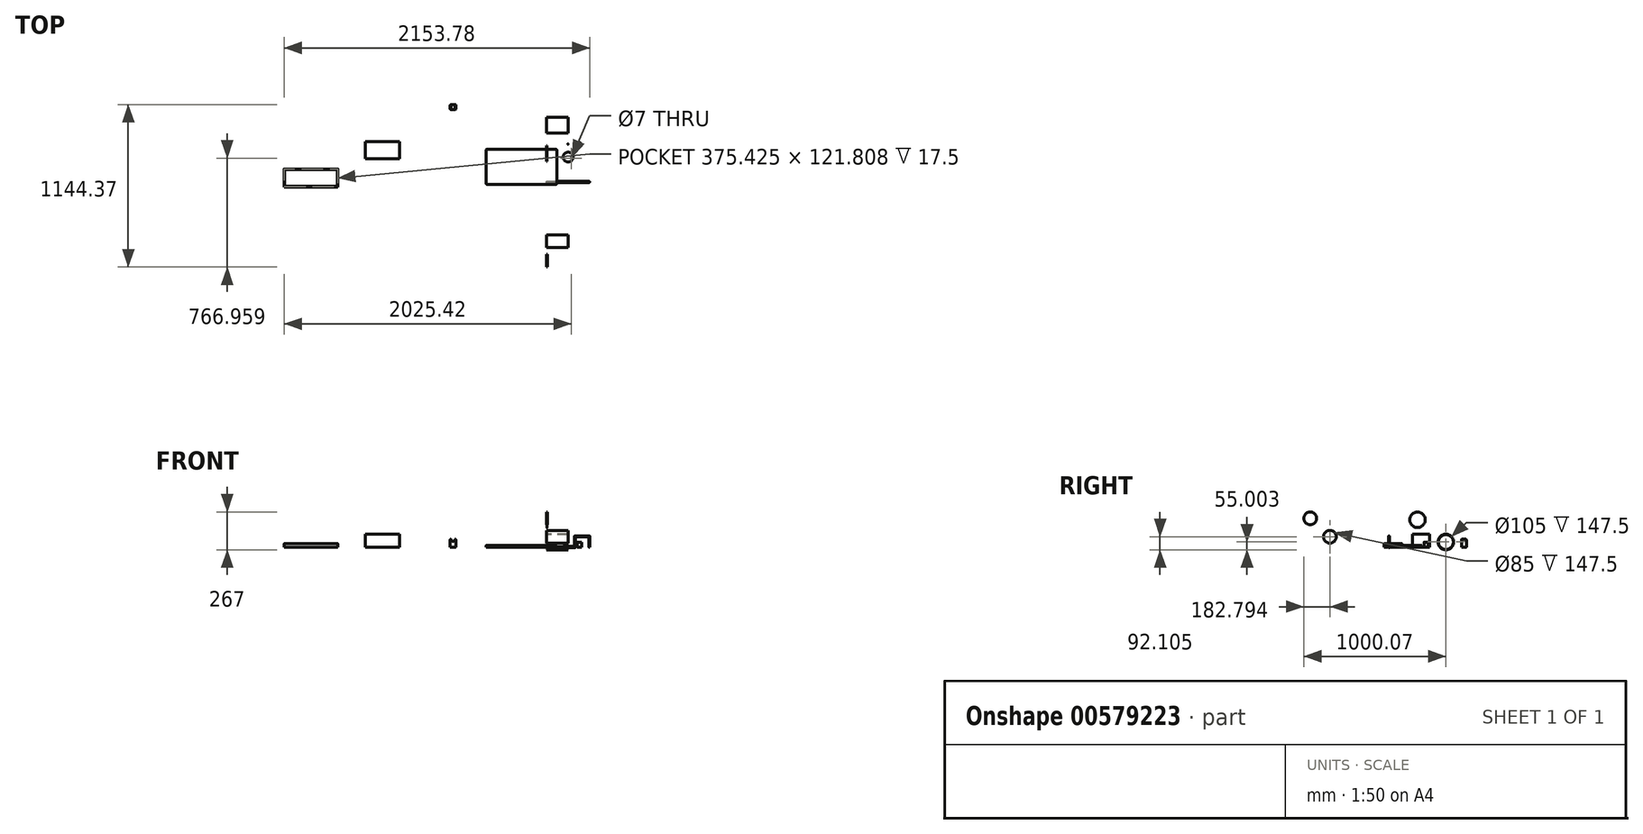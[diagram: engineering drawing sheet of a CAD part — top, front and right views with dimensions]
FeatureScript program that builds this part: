
annotation { "Feature Type Name" : "Feature", "Feature Type Description" : "" }
export const myFeature = defineFeature(function(context is Context, id is Id, definition is map)
    precondition{}
    {
        {
            var Q0;
            Q0=qCreatedBy(makeId("Top.planeOp"),FACE);
            var sketch = newSketch(context, id + "F0", { "sketchPlane" : qUnion([Q0])});
            skLineSegment(sketch, "E0.bottom", {"start": v(-427.44, 231.54) * mm, "end": v(72.56, 231.54) * mm});
            skLineSegment(sketch, "E0.top", {"start": v(-427.44, -18.46) * mm, "end": v(72.56, -18.46) * mm});
            skLineSegment(sketch, "E0.left", {"start": v(-427.44, 231.54) * mm, "end": v(-427.44, -18.46) * mm});
            skLineSegment(sketch, "E0.right", {"start": v(72.56, 231.54) * mm, "end": v(72.56, -18.46) * mm});
            skSolve(sketch);
        }
        {
            var Q0;
            Q0=makeQuery(id+"F0.imprint","IMPRINT",FACE,{"disambiguationData":[TD([[makeQuery(id+"F0.imprint","IMPRINT",EDGE,{"derivedFrom":sQuery(id+"F0.wireOp",EDGE,"E0.bottom")}),-1.0]])]});
            extrude(context, id + "F1", {"entities" : qUnion([Q0]), "depth" : 10 * mm, "offsetDistance" : 25 * mm});
        }
        {
            var Q0;
            Q0=qCreatedBy(makeId("Right.planeOp"),FACE);
            var sketch = newSketch(context, id + "F2", { "sketchPlane" : qUnion([Q0])});
            skCircle(sketch, "E1", {"center": v(400.53, 35.64) * mm, "radius": 55 * mm});
            skSolve(sketch);
        }
        {
            var Q0;
            Q0=makeQuery(id+"F2.imprint","IMPRINT",FACE,{"disambiguationData":[TD([[makeQuery(id+"F2.imprint","IMPRINT",EDGE,{"derivedFrom":sQuery(id+"F2.wireOp",EDGE,"E1")}),1.0]])]});
            extrude(context, id + "F3", {"entities" : qUnion([Q0]), "depth" : 150 * mm, "offsetDistance" : 25 * mm});
        }
        {
            var Q0;
            Q0=makeQuery(id+"F3.opExtrude","CAP_FACE",FACE,{"disambiguationData":[OSD([sQuery(id+"F2.wireOp",EDGE,"E1")])],"isStart":false});
            shell(context, id + "F4", {"entities" : qUnion([Q0]), "thickness" : 2.5 * mm});
        }
        {
            var Q0;
            Q0=makeQuery(id+"F1.opExtrude","SWEPT_EDGE",EDGE,{"disambiguationData":[OSD([sQuery(id+"F0.wireOp",EDGE,"E0.bottom"),sQuery(id+"F0.wireOp",EDGE,"E0.right")])]});
            var Q1;
            Q1=makeQuery(id+"F1.opExtrude","SWEPT_EDGE",EDGE,{"disambiguationData":[OSD([sQuery(id+"F0.wireOp",EDGE,"E0.bottom"),sQuery(id+"F0.wireOp",EDGE,"E0.left")])]});
            var Q2;
            Q2=makeQuery(id+"F1.opExtrude","SWEPT_EDGE",EDGE,{"disambiguationData":[OSD([sQuery(id+"F0.wireOp",EDGE,"E0.top"),sQuery(id+"F0.wireOp",EDGE,"E0.left")])]});
            var Q3;
            Q3=makeQuery(id+"F1.opExtrude","SWEPT_EDGE",EDGE,{"disambiguationData":[OSD([sQuery(id+"F0.wireOp",EDGE,"E0.top"),sQuery(id+"F0.wireOp",EDGE,"E0.right")])]});
            fillet(context, id + "F5", {"entities" : qUnion([Q0, Q1, Q2, Q3]), "radius" : 10 * mm, "tangentPropagation" : true, "allowEdgeOverflow" : false});
        }
        {
            var Q0;
            Q0=qCreatedBy(makeId("Right.planeOp"),FACE);
            var sketch = newSketch(context, id + "F6", { "sketchPlane" : qUnion([Q0])});
            skCircle(sketch, "E2", {"center": v(200.54, 191.77) * mm, "radius": 54.75 * mm});
            skSolve(sketch);
        }
        {
            var Q0;
            Q0 = qSketchRegion(id + "F6", true);
            extrude(context, id + "F7", {"entities" : qUnion([Q0]), "depth" : 3 * mm, "offsetDistance" : 25 * mm});
        }
        {
            var Q0;
            Q0=qCreatedBy(makeId("Front.planeOp"),FACE);
            var sketch = newSketch(context, id + "F8", { "sketchPlane" : qUnion([Q0])});
            skLineSegment(sketch, "E3", {"start": v(0, 0) * mm, "end": v(200, 0) * mm});
            skLineSegment(sketch, "E4", {"start": v(200, 0) * mm, "end": v(200, 75) * mm});
            skLineSegment(sketch, "E5", {"start": v(200, 75) * mm, "end": v(300, 75) * mm});
            skLineSegment(sketch, "E6", {"start": v(300, 75) * mm, "end": v(300, 0) * mm});
            skSolve(sketch);
        }
        {
            var Q0;
            Q0=qCreatedBy(makeId("Right.planeOp"),FACE);
            var sketch = newSketch(context, id + "F9", { "sketchPlane" : qUnion([Q0])});
            skCircle(sketch, "E7", {"center": v(0, 0) * mm, "radius": 3.5 * mm});
            skSolve(sketch);
        }
        {
            var Q0;
            Q0=makeQuery(id+"F9.imprint","IMPRINT",FACE,{"disambiguationData":[TD([[makeQuery(id+"F9.imprint","IMPRINT",EDGE,{"derivedFrom":sQuery(id+"F9.wireOp",EDGE,"E7")}),1.0]])]});
            var Q1;
            Q1=sQuery(id+"F8.wireOp",EDGE,"E3");
            var Q2;
            Q2=sQuery(id+"F8.wireOp",EDGE,"E4");
            var Q3;
            Q3=sQuery(id+"F8.wireOp",EDGE,"E5");
            var Q4;
            Q4=sQuery(id+"F8.wireOp",EDGE,"E6");
            sweep(context, id + "F10", {"profiles" : qUnion([Q0]), "path" : qUnion([Q1, Q2, Q3, Q4])});
        }
        {
            var Q0;
            Q0=qCreatedBy(makeId("Top.planeOp"),FACE);
            var sketch = newSketch(context, id + "F11", { "sketchPlane" : qUnion([Q0])});
            skCircle(sketch, "E8", {"center": v(151.31, 175.12) * mm, "radius": 35 * mm});
            skSolve(sketch);
        }
        {
            var Q0;
            Q0=makeQuery(id+"F11.imprint","IMPRINT",FACE,{"disambiguationData":[TD([[makeQuery(id+"F11.imprint","IMPRINT",EDGE,{"derivedFrom":sQuery(id+"F11.wireOp",EDGE,"E8")}),1.0]])]});
            extrude(context, id + "F12", {"entities" : qUnion([Q0]), "depth" : 5 * mm, "offsetDistance" : 25 * mm});
        }
        {
            var Q0;
            Q0=qCreatedBy(makeId("Top.planeOp"),FACE);
            var sketch = newSketch(context, id + "F13", { "sketchPlane" : qUnion([Q0])});
            skCircle(sketch, "E9", {"center": v(230.62, 261.74) * mm, "radius": 15 * mm});
            skSolve(sketch);
        }
        {
            var Q0;
            Q0=makeQuery(id+"F13.imprint","IMPRINT",FACE,{"disambiguationData":[TD([[makeQuery(id+"F13.imprint","IMPRINT",EDGE,{"derivedFrom":sQuery(id+"F13.wireOp",EDGE,"E9")}),1.0]])]});
            extrude(context, id + "F14", {"entities" : qUnion([Q0]), "depth" : 35 * mm, "offsetDistance" : 25 * mm});
        }
        {
            var Q0;
            Q0=qCreatedBy(makeId("Top.planeOp"),FACE);
            var sketch = newSketch(context, id + "F15", { "sketchPlane" : qUnion([Q0])});
            skCircle(sketch, "E10", {"center": v(150.44, 267.16) * mm, "radius": 2.5 * mm});
            skSolve(sketch);
        }
        {
            var Q0;
            Q0=makeQuery(id+"F15.imprint","IMPRINT",FACE,{"disambiguationData":[TD([[makeQuery(id+"F15.imprint","IMPRINT",EDGE,{"derivedFrom":sQuery(id+"F15.wireOp",EDGE,"E10")}),1.0]])]});
            extrude(context, id + "F16", {"entities" : qUnion([Q0]), "depth" : 5 * mm, "offsetDistance" : 25 * mm});
        }
        {
            var Q0;
            Q0=qCreatedBy(makeId("Top.planeOp"),FACE);
            var sketch = newSketch(context, id + "F17", { "sketchPlane" : qUnion([Q0])});
            skLineSegment(sketch, "E11.bottom", {"start": v(-639.12, 509.83) * mm, "end": v(-679.12, 509.83) * mm});
            skLineSegment(sketch, "E11.top", {"start": v(-639.12, 544.83) * mm, "end": v(-679.12, 544.83) * mm});
            skLineSegment(sketch, "E11.left", {"start": v(-639.12, 509.83) * mm, "end": v(-639.12, 544.83) * mm});
            skLineSegment(sketch, "E11.right", {"start": v(-679.12, 509.83) * mm, "end": v(-679.12, 544.83) * mm});
            skPoint(sketch, "E11.middle", {"position": v(-659.12, 527.33) * mm});
            skSolve(sketch);
        }
        {
            var Q0;
            Q0=makeQuery(id+"F17.imprint","IMPRINT",FACE,{"disambiguationData":[TD([[makeQuery(id+"F17.imprint","IMPRINT",EDGE,{"derivedFrom":sQuery(id+"F17.wireOp",EDGE,"E11.bottom")}),-1.0]])]});
            extrude(context, id + "F18", {"entities" : qUnion([Q0]), "depth" : 55 * mm, "offsetDistance" : 25 * mm});
        }
        {
            var Q0;
            Q0=makeQuery(id+"F18.opExtrude","SWEPT_FACE",FACE,{"disambiguationData":[OSD([sQuery(id+"F17.wireOp",EDGE,"E11.bottom")])]});
            var sketch = newSketch(context, id + "F19", { "sketchPlane" : qUnion([Q0])});
            skArc(sketch, "E12", {"start": v(-674.12, 55) * mm, "mid": v(-659.12, 39.88) * mm, "end": v(-644.12, 55) * mm});
            skSolve(sketch);
        }
        {
            var Q0;
            {var subQ0=sQuery(id+"F19.wireOp",EDGE,"E12");Q0=makeQuery(id+"F19.imprint","IMPRINT",FACE,{"disambiguationData":[TD([[makeQuery(id+"F19.imprint","IMPRINT",EDGE,{"derivedFrom":subQ0}),1.0]])]});}
            extrude(context, id + "F20", {"entities" : qUnion([Q0]), "operationType" : NewBodyOperationType.REMOVE, "oppositeDirection" : true, "depth" : 40 * mm, "offsetDistance" : 25 * mm});
        }
        {
            var Q0;
            Q0=makeQuery(id+"F18.opExtrude","CAP_EDGE",EDGE,{"disambiguationData":[OSD([sQuery(id+"F17.wireOp",EDGE,"E11.right")])],"isStart":false});
            var Q1;
            {var subQ0=sQuery(id+"F17.wireOp",EDGE,"E11.bottom");var subQ1=sQuery(id+"F17.wireOp",EDGE,"E11.right");Q1=makeQuery(id+"F20.boolean.opBoolean","SPLIT",EDGE,{"disambiguationData":[TD([makeQuery(id+"F18.opExtrude","SWEPT_FACE",FACE,{"disambiguationData":[OSD([subQ1])]})])],"derivedFrom":makeQuery(id+"F18.opExtrude","CAP_EDGE",EDGE,{"disambiguationData":[OSD([subQ0])],"isStart":false})});}
            var Q2;
            Q2=makeQuery(id+"F18.opExtrude","SWEPT_EDGE",EDGE,{"disambiguationData":[OSD([sQuery(id+"F17.wireOp",EDGE,"E11.bottom"),sQuery(id+"F17.wireOp",EDGE,"E11.right")])]});
            var Q3;
            Q3=makeQuery(id+"F18.opExtrude","SWEPT_EDGE",EDGE,{"disambiguationData":[OSD([sQuery(id+"F17.wireOp",EDGE,"E11.bottom"),sQuery(id+"F17.wireOp",EDGE,"E11.left")])]});
            var Q4;
            {var subQ0=sQuery(id+"F17.wireOp",EDGE,"E11.bottom");var subQ1=sQuery(id+"F17.wireOp",EDGE,"E11.left");Q4=makeQuery(id+"F20.boolean.opBoolean","SPLIT",EDGE,{"disambiguationData":[TD([makeQuery(id+"F18.opExtrude","SWEPT_FACE",FACE,{"disambiguationData":[OSD([subQ1])]})])],"derivedFrom":makeQuery(id+"F18.opExtrude","CAP_EDGE",EDGE,{"disambiguationData":[OSD([subQ0])],"isStart":false})});}
            var Q5;
            Q5=makeQuery(id+"F18.opExtrude","SWEPT_EDGE",EDGE,{"disambiguationData":[OSD([sQuery(id+"F17.wireOp",EDGE,"E11.top"),sQuery(id+"F17.wireOp",EDGE,"E11.left")])]});
            var Q6;
            Q6=makeQuery(id+"F18.opExtrude","CAP_EDGE",EDGE,{"disambiguationData":[OSD([sQuery(id+"F17.wireOp",EDGE,"E11.left")])],"isStart":false});
            var Q7;
            {var subQ0=sQuery(id+"F17.wireOp",EDGE,"E11.left");var subQ1=sQuery(id+"F17.wireOp",EDGE,"E11.top");Q7=makeQuery(id+"F20.boolean.opBoolean","SPLIT",EDGE,{"disambiguationData":[TD([makeQuery(id+"F18.opExtrude","SWEPT_FACE",FACE,{"disambiguationData":[OSD([subQ0])]})])],"derivedFrom":makeQuery(id+"F18.opExtrude","CAP_EDGE",EDGE,{"disambiguationData":[OSD([subQ1])],"isStart":false})});}
            var Q8;
            {var subQ0=sQuery(id+"F17.wireOp",EDGE,"E11.right");var subQ1=sQuery(id+"F17.wireOp",EDGE,"E11.top");Q8=makeQuery(id+"F20.boolean.opBoolean","SPLIT",EDGE,{"disambiguationData":[TD([makeQuery(id+"F18.opExtrude","SWEPT_FACE",FACE,{"disambiguationData":[OSD([subQ0])]})])],"derivedFrom":makeQuery(id+"F18.opExtrude","CAP_EDGE",EDGE,{"disambiguationData":[OSD([subQ1])],"isStart":false})});}
            var Q9;
            Q9=makeQuery(id+"F18.opExtrude","SWEPT_EDGE",EDGE,{"disambiguationData":[OSD([sQuery(id+"F17.wireOp",EDGE,"E11.top"),sQuery(id+"F17.wireOp",EDGE,"E11.right")])]});
            fillet(context, id + "F21", {"entities" : qUnion([Q0, Q1, Q2, Q3, Q4, Q5, Q6, Q7, Q8, Q9]), "radius" : 5 * mm, "tangentPropagation" : true, "allowEdgeOverflow" : false});
        }
        {
            var Q0;
            Q0=makeQuery(id+"F12.opExtrude","CAP_FACE",FACE,{"disambiguationData":[OSD([sQuery(id+"F11.wireOp",EDGE,"E8")])],"isStart":true});
            var sketch = newSketch(context, id + "F22", { "sketchPlane" : qUnion([Q0])});
            skPoint(sketch, "E13", {"position": v(175.14, -167.42) * mm});
            skSolve(sketch);
        }
        {
            var Q0;
            Q0=sQuery(id+"F22.wireOp",VERTEX,"E13");
            var Q1;
            Q1=makeQuery(id+"F12.opExtrude","SWEPT_BODY",BODY,{"disambiguationData":[OSD([sQuery(id+"F11.wireOp",EDGE,"E8")])]});
            hole(context, id + "F23", {"style" : HoleStyle.SIMPLE, "endStyle" : HoleEndStyle.THROUGH, "holeDiameter" : 7 * mm, "majorDiameter" : 5 * mm, "tappedDepth" : 12.6 * mm, "tapClearance" : 3, "locations" : qUnion([Q0]), "scope" : qUnion([Q1])});
        }
        {
            var Q0;
            Q0=qCreatedBy(makeId("Top.planeOp"),FACE);
            var sketch = newSketch(context, id + "F24", { "sketchPlane" : qUnion([Q0])});
            skLineSegment(sketch, "E14.bottom", {"start": v(-1036.13, 164.62) * mm, "end": v(-1276.13, 164.62) * mm});
            skLineSegment(sketch, "E14.top", {"start": v(-1036.13, 284.62) * mm, "end": v(-1276.13, 284.62) * mm});
            skLineSegment(sketch, "E14.left", {"start": v(-1036.13, 164.62) * mm, "end": v(-1036.13, 284.62) * mm});
            skLineSegment(sketch, "E14.right", {"start": v(-1276.13, 164.62) * mm, "end": v(-1276.13, 284.62) * mm});
            skPoint(sketch, "E14.middle", {"position": v(-1156.13, 224.62) * mm});
            skSolve(sketch);
        }
        {
            var Q0;
            Q0=makeQuery(id+"F24.imprint","IMPRINT",FACE,{"disambiguationData":[TD([[makeQuery(id+"F24.imprint","IMPRINT",EDGE,{"derivedFrom":sQuery(id+"F24.wireOp",EDGE,"E14.bottom")}),-1.0]])]});
            extrude(context, id + "F25", {"entities" : qUnion([Q0]), "depth" : 90 * mm, "offsetDistance" : 25 * mm});
        }
        {
            var Q0;
            Q0=qCreatedBy(makeId("Right.planeOp"),FACE);
            var sketch = newSketch(context, id + "F26", { "sketchPlane" : qUnion([Q0])});
            skCircle(sketch, "E15", {"center": v(-416.75, 72.74) * mm, "radius": 45 * mm});
            skSolve(sketch);
        }
        {
            var Q0;
            Q0=makeQuery(id+"F26.imprint","IMPRINT",FACE,{"disambiguationData":[TD([[makeQuery(id+"F26.imprint","IMPRINT",EDGE,{"derivedFrom":sQuery(id+"F26.wireOp",EDGE,"E15")}),1.0]])]});
            extrude(context, id + "F27", {"entities" : qUnion([Q0]), "depth" : 150 * mm, "offsetDistance" : 25 * mm});
        }
        {
            var Q0;
            Q0=makeQuery(id+"F27.opExtrude","CAP_FACE",FACE,{"disambiguationData":[OSD([sQuery(id+"F26.wireOp",EDGE,"E15")])],"isStart":true});
            shell(context, id + "F28", {"entities" : qUnion([Q0]), "thickness" : 2.5 * mm});
        }
        {
            var Q0;
            Q0=qCreatedBy(makeId("Right.planeOp"),FACE);
            var sketch = newSketch(context, id + "F29", { "sketchPlane" : qUnion([Q0])});
            skCircle(sketch, "E16", {"center": v(-554.54, 202.64) * mm, "radius": 45 * mm});
            skSolve(sketch);
        }
        {
            var Q0;
            Q0=makeQuery(id+"F29.imprint","IMPRINT",FACE,{"disambiguationData":[TD([[makeQuery(id+"F29.imprint","IMPRINT",EDGE,{"derivedFrom":sQuery(id+"F29.wireOp",EDGE,"E16")}),1.0]])]});
            extrude(context, id + "F30", {"entities" : qUnion([Q0]), "depth" : 5 * mm, "offsetDistance" : 25 * mm});
        }
        {
            var Q0;
            Q0=qCreatedBy(makeId("Top.planeOp"),FACE);
            var sketch = newSketch(context, id + "F31", { "sketchPlane" : qUnion([Q0])});
            skLineSegment(sketch, "E17.bottom", {"start": v(-1469.85, -35.08) * mm, "end": v(-1850.28, -35.08) * mm});
            skLineSegment(sketch, "E17.top", {"start": v(-1469.85, 91.73) * mm, "end": v(-1850.28, 91.73) * mm});
            skLineSegment(sketch, "E17.left", {"start": v(-1469.85, -35.08) * mm, "end": v(-1469.85, 91.73) * mm});
            skLineSegment(sketch, "E17.right", {"start": v(-1850.28, -35.08) * mm, "end": v(-1850.28, 91.73) * mm});
            skPoint(sketch, "E17.middle", {"position": v(-1660.07, 28.32) * mm});
            skSolve(sketch);
        }
        {
            var Q0;
            Q0=makeQuery(id+"F31.imprint","IMPRINT",FACE,{"disambiguationData":[TD([[makeQuery(id+"F31.imprint","IMPRINT",EDGE,{"derivedFrom":sQuery(id+"F31.wireOp",EDGE,"E17.bottom")}),-1.0]])]});
            extrude(context, id + "F32", {"entities" : qUnion([Q0]), "depth" : 25 * mm, "offsetDistance" : 25 * mm});
        }
        {
            var Q0;
            Q0=makeQuery(id+"F32.opExtrude","CAP_EDGE",EDGE,{"disambiguationData":[OSD([sQuery(id+"F31.wireOp",EDGE,"E17.bottom")])],"isStart":false});
            var Q1;
            Q1=makeQuery(id+"F32.opExtrude","CAP_EDGE",EDGE,{"disambiguationData":[OSD([sQuery(id+"F31.wireOp",EDGE,"E17.left")])],"isStart":false});
            var Q2;
            Q2=makeQuery(id+"F32.opExtrude","CAP_FACE",FACE,{"disambiguationData":[OSD([sQuery(id+"F31.wireOp",EDGE,"E17.bottom"),sQuery(id+"F31.wireOp",EDGE,"E17.top"),sQuery(id+"F31.wireOp",EDGE,"E17.left"),sQuery(id+"F31.wireOp",EDGE,"E17.right")])],"isStart":false});
            fillet(context, id + "F33", {"entities" : qUnion([Q0, Q1, Q2]), "tangentPropagation" : true, "radius" : 5 * mm, "defaultsChanged" : false, "vertexSettings" : [], "allowEdgeOverflow" : false});
        }
        {
            var Q0;
            Q0=makeQuery(id+"F32.opExtrude","CAP_FACE",FACE,{"disambiguationData":[OSD([sQuery(id+"F31.wireOp",EDGE,"E17.bottom"),sQuery(id+"F31.wireOp",EDGE,"E17.top"),sQuery(id+"F31.wireOp",EDGE,"E17.left"),sQuery(id+"F31.wireOp",EDGE,"E17.right")])],"isStart":false});
            shell(context, id + "F34", {"entities" : qUnion([Q0]), "thickness" : 2.5 * mm});
        }
    });
